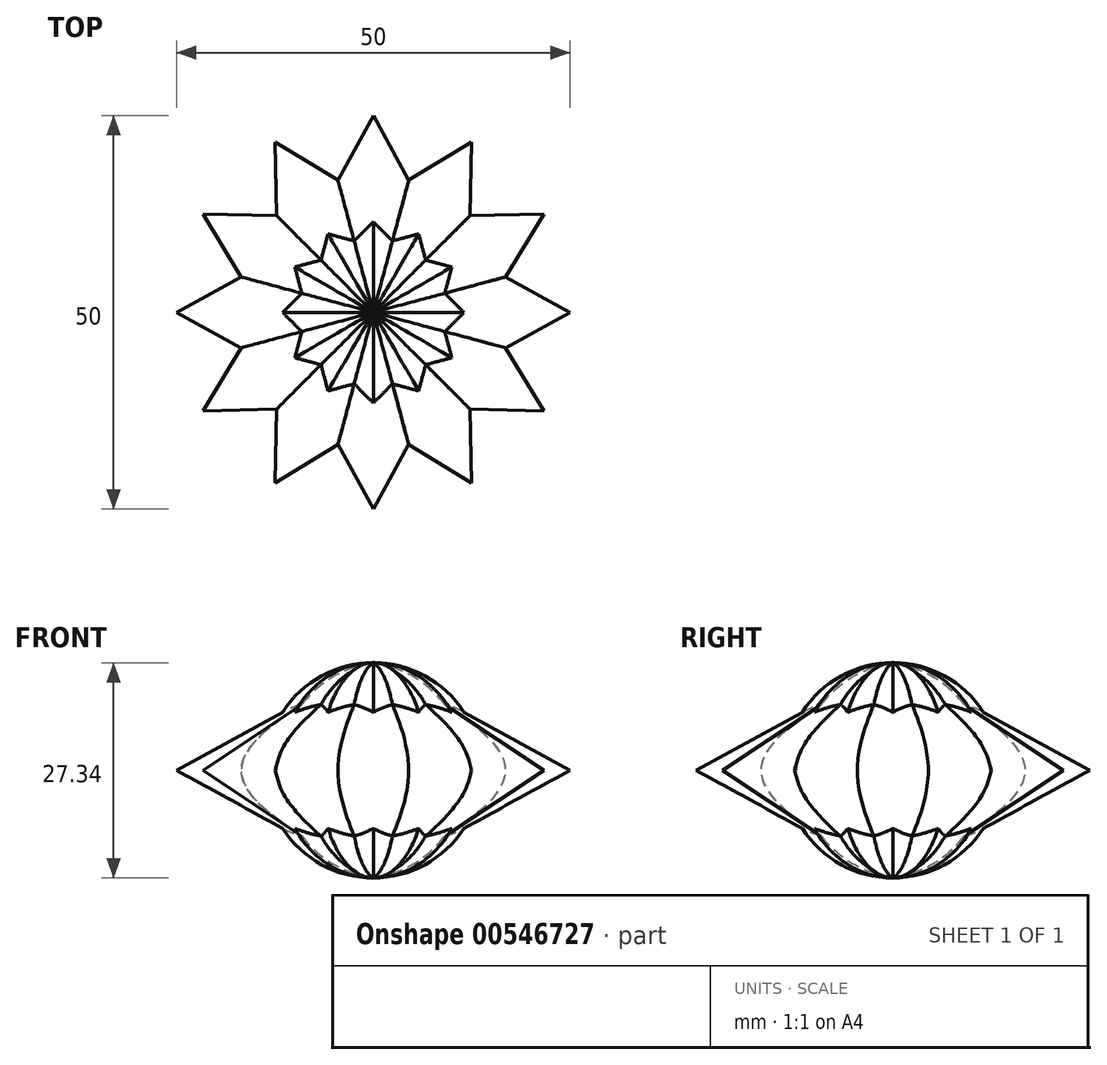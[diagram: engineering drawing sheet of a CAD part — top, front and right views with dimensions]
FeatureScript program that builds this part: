
annotation { "Feature Type Name" : "Feature", "Feature Type Description" : "" }
export const myFeature = defineFeature(function(context is Context, id is Id, definition is map)
    precondition{}
    {
        {
            var Q0;
            Q0=qCreatedBy(makeId("Front.planeOp"),FACE);
            var sketch = newSketch(context, id + "F0", { "sketchPlane" : qUnion([Q0])});
            skLineSegment(sketch, "E0", {"start": v(0, 0) * mm, "end": v(0, 13.67) * mm});
            skLineSegment(sketch, "E1", {"start": v(0, 0) * mm, "end": v(-25, 0) * mm});
            skLineSegment(sketch, "E2", {"start": v(0, 13.67) * mm, "end": v(-25, 0) * mm});
            skSolve(sketch);
        }
        {
            var Q0;
            Q0=makeQuery(id+"F0.imprint","IMPRINT",FACE,{"disambiguationData":[TD([[makeQuery(id+"F0.imprint","IMPRINT",EDGE,{"derivedFrom":sQuery(id+"F0.wireOp",EDGE,"E0")}),1.0]])]});
            var Q1;
            Q1=sQuery(id+"F0.wireOp",EDGE,"E1");
            revolve(context, id + "F1", {"entities" : qUnion([Q0]), "axis" : qUnion([Q1]), "revolveType" : RevolveType.FULL});
        }
        {
            var Q0;
            Q0=makeQuery(id+"F1.opRevolve","SWEPT_BODY",BODY,{"disambiguationData":[OSD([sQuery(id+"F0.wireOp",EDGE,"E0"),sQuery(id+"F0.wireOp",EDGE,"E1"),sQuery(id+"F0.wireOp",EDGE,"E2")])]});
            var Q1;
            Q1=sQuery(id+"F0.wireOp",EDGE,"E0");
            var Q2;
            Q2=makeQuery(id+"F1.opRevolve","SWEPT_BODY",BODY,{"disambiguationData":[OSD([sQuery(id+"F0.wireOp",EDGE,"E0"),sQuery(id+"F0.wireOp",EDGE,"E1"),sQuery(id+"F0.wireOp",EDGE,"E2")])]});
            circularPattern(context, id + "F2", {"operationType" : NewBodyOperationType.ADD, "entities" : qUnion([Q0]), "axis" : qUnion([Q1]), "angle" : 360 * degree, "instanceCount" : 12, "equalSpace" : true});
        }
    });
